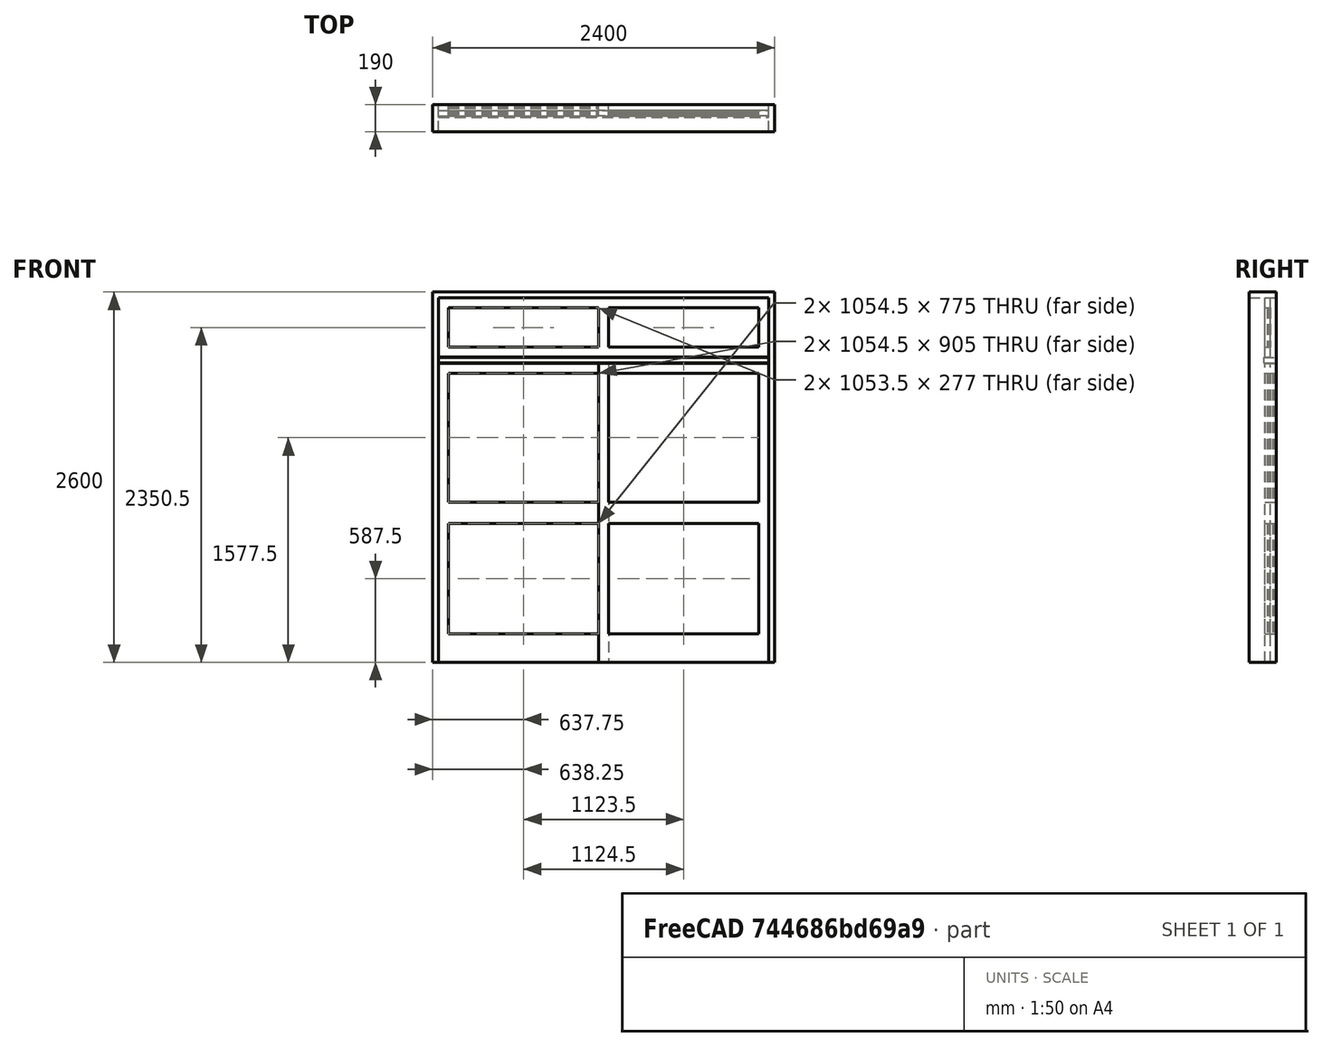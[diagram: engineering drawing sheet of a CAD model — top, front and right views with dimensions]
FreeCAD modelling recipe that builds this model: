
FCSTD DOCUMENT  (FreeCAD 0.16R6704 (Git))
Label: slinding double doors with glass and transom
License: CreativeCommons Attribution
LicenseURL: http://creativecommons.org/licenses/by/4.0/
objects: Sketcher::SketchObject×1, Part::FeaturePython×1
note: 2 computed .brp shape members not serialized (recipe doc carries the construction recipe); baked Part::Feature solids carry a one-line shape summary decoded from their .brp

FEATURE [Sketcher::SketchObject] Sketch180
  Placement = pos=(0,0,0) rot=(1,0,0;1.5708rad)
  sketch-geometry (50):
    g0: LineSegment StartX=0 StartY=0 StartZ=0 EndX=2400 EndY=0 EndZ=0
    g1: LineSegment StartX=2400 StartY=0 StartZ=0 EndX=2400 EndY=2600 EndZ=0
    g2: LineSegment StartX=2400 StartY=2600 StartZ=0 EndX=0 EndY=2600 EndZ=0
    g3: LineSegment StartX=0 StartY=2600 StartZ=0 EndX=0 EndY=0 EndZ=0
    g4: LineSegment StartX=40 StartY=0 StartZ=0 EndX=2360 EndY=0 EndZ=0
    g5: LineSegment StartX=2360 StartY=0 StartZ=0 EndX=2360 EndY=2560 EndZ=0
    g6: LineSegment StartX=2360 StartY=2560 StartZ=0 EndX=40 EndY=2560 EndZ=0
    g7: LineSegment StartX=40 StartY=2560 StartZ=0 EndX=40 EndY=0 EndZ=0
    g8: LineSegment StartX=111 StartY=2030 StartZ=0 EndX=1165.5 EndY=2030 EndZ=0
    g9: LineSegment StartX=1165.5 StartY=2030 StartZ=0 EndX=1165.5 EndY=1125 EndZ=0
    g10: LineSegment StartX=1165.5 StartY=1125 StartZ=0 EndX=111 EndY=1125 EndZ=0
    g11: LineSegment StartX=111 StartY=1125 StartZ=0 EndX=111 EndY=2030 EndZ=0
    g12: LineSegment StartX=111 StartY=975 StartZ=0 EndX=1165.5 EndY=975 EndZ=0
    g13: LineSegment StartX=1165.5 StartY=975 StartZ=0 EndX=1165.5 EndY=200 EndZ=0
    g14: LineSegment StartX=1165.5 StartY=200 StartZ=0 EndX=111 EndY=200 EndZ=0
    g15: LineSegment StartX=111 StartY=200 StartZ=0 EndX=111 EndY=975 EndZ=0
    g16: LineSegment [constr] StartX=-278 StartY=1050 StartZ=0 EndX=2205 EndY=1050 EndZ=0
    g17: LineSegment StartX=41 StartY=2100 StartZ=0 EndX=1235.5 EndY=2100 EndZ=0
    g18: LineSegment StartX=1235.5 StartY=2100 StartZ=0 EndX=1235.5 EndY=1 EndZ=0
    g19: LineSegment StartX=1235.5 StartY=1 StartZ=0 EndX=41 EndY=1 EndZ=0
    g20: LineSegment StartX=41 StartY=1 StartZ=0 EndX=41 EndY=2100 EndZ=0
    g21: LineSegment [constr] StartX=1200 StartY=2318.59 StartZ=0 EndX=1200 EndY=-187.261 EndZ=0
    g22: LineSegment StartX=2289 StartY=2030 StartZ=0 EndX=1234.5 EndY=2030 EndZ=0
    g23: LineSegment StartX=1234.5 StartY=2030 StartZ=0 EndX=1234.5 EndY=1125 EndZ=0
    g24: LineSegment StartX=1234.5 StartY=1125 StartZ=0 EndX=2289 EndY=1125 EndZ=0
    g25: LineSegment StartX=2289 StartY=1125 StartZ=0 EndX=2289 EndY=2030 EndZ=0
    g26: LineSegment StartX=2289 StartY=975 StartZ=0 EndX=1234.5 EndY=975 EndZ=0
    g27: LineSegment StartX=1234.5 StartY=975 StartZ=0 EndX=1234.5 EndY=200 EndZ=0
    g28: LineSegment StartX=1234.5 StartY=200 StartZ=0 EndX=2289 EndY=200 EndZ=0
    g29: LineSegment StartX=2289 StartY=200 StartZ=0 EndX=2289 EndY=975 EndZ=0
    g30: LineSegment StartX=2359 StartY=2100 StartZ=0 EndX=1164.5 EndY=2100 EndZ=0
    g31: LineSegment StartX=1164.5 StartY=2100 StartZ=0 EndX=1164.5 EndY=1 EndZ=0
    g32: LineSegment StartX=1164.5 StartY=1 StartZ=0 EndX=2359 EndY=1 EndZ=0
    g33: LineSegment StartX=2359 StartY=1 StartZ=0 EndX=2359 EndY=2100 EndZ=0
    g34: LineSegment StartX=41 StartY=2559 StartZ=0 EndX=2359 EndY=2559 EndZ=0
    g35: LineSegment StartX=2359 StartY=2559 StartZ=0 EndX=2359 EndY=2142 EndZ=0
    g36: LineSegment StartX=2359 StartY=2142 StartZ=0 EndX=41 EndY=2142 EndZ=0
    g37: LineSegment StartX=41 StartY=2142 StartZ=0 EndX=41 EndY=2559 EndZ=0
    g38: LineSegment StartX=111 StartY=2489 StartZ=0 EndX=1164.5 EndY=2489 EndZ=0
    g39: LineSegment StartX=1164.5 StartY=2489 StartZ=0 EndX=1164.5 EndY=2212 EndZ=0
    g40: LineSegment StartX=1164.5 StartY=2212 StartZ=0 EndX=111 EndY=2212 EndZ=0
    g41: LineSegment StartX=111 StartY=2212 StartZ=0 EndX=111 EndY=2489 EndZ=0
    g42: LineSegment StartX=1235.5 StartY=2489 StartZ=0 EndX=2289 EndY=2489 EndZ=0
    g43: LineSegment StartX=2289 StartY=2489 StartZ=0 EndX=2289 EndY=2212 EndZ=0
    g44: LineSegment StartX=2289 StartY=2212 StartZ=0 EndX=1235.5 EndY=2212 EndZ=0
    g45: LineSegment StartX=1235.5 StartY=2212 StartZ=0 EndX=1235.5 EndY=2489 EndZ=0
    g46: LineSegment StartX=41 StartY=2141 StartZ=0 EndX=2359 EndY=2141 EndZ=0
    g47: LineSegment StartX=2359 StartY=2141 StartZ=0 EndX=2359 EndY=2101 EndZ=0
    g48: LineSegment StartX=2359 StartY=2101 StartZ=0 EndX=41 EndY=2101 EndZ=0
    g49: LineSegment StartX=41 StartY=2101 StartZ=0 EndX=41 EndY=2141 EndZ=0
  constraints (146):
    c: Coincident(g0,g1)
    c: Coincident(g1,g2)
    c: Coincident(g2,g3)
    c: Coincident(g3,g0)
    c: Horizontal(g0)
    c: Horizontal(g2)
    c: Vertical(g1)
    c: Vertical(g3)
    c: Coincident(g4,g5)
    c: Coincident(g5,g6)
    c: Coincident(g6,g7)
    c: Coincident(g7,g4)
    c: Horizontal(g4)
    c: Horizontal(g6)
    c: Vertical(g5)
    c: Vertical(g7)
    c: DistanceY(g1) = 2600  'Altura do vão'
    c: DistanceX(g0) = 2400  'Largura do vão'
    c: DistanceY(g6,g2) = 40  'Altura batente superior'
    c: DistanceX(g2,g6) = 40  'Largura do batente 1'
    c: DistanceX(g4,g0) = 40  'Largura do batente 2'
    c: DistanceY(g0,g4) = 0
    c: Coincident(g0,g-1)
    c: Coincident(g8,g9)
    c: Coincident(g9,g10)
    c: Coincident(g10,g11)
    c: Coincident(g11,g8)
    c: Horizontal(g8)
    c: Horizontal(g10)
    c: Vertical(g9)
    c: Vertical(g11)
    c: Coincident(g12,g13)
    c: Coincident(g13,g14)
    c: Coincident(g14,g15)
    c: Coincident(g15,g12)
    c: Horizontal(g12)
    c: Horizontal(g14)
    c: Vertical(g13)
    c: Vertical(g15)
    c: DistanceX(g10,g12) = 0
    c: DistanceX(g9,g12) = 0
    c: DistanceY(g12,g10) = 150  'Altura do montante intermediário porta'
    c: DistanceY(g-1,g14) = 200  'Altura moldura inferior porta'
    c: Horizontal(g16)
    c: Symmetric(g10,g12,g16)
    c: DistanceY(g-1,g16) = 1050  'Altura da divisão intermediária porta'
    c: Coincident(g17,g18)
    c: Coincident(g18,g19)
    c: Coincident(g19,g20)
    c: Horizontal(g17)
    c: Horizontal(g19)
    c: Vertical(g18)
    c: Vertical(g20)
    c: DistanceY(g4,g18) = 1
    c: DistanceX(g6,g17) = 1
    c: Vertical(g21)  'Constraint59'
    c: Symmetric(g2,g1,g21)  'Constraint58'
    c: Coincident(g22,g23)
    c: Coincident(g23,g24)
    c: Coincident(g24,g25)
    c: Coincident(g25,g22)
    c: Horizontal(g22)
    c: Horizontal(g24)
    c: Vertical(g23)
    c: Vertical(g25)
    c: Coincident(g26,g27)
    c: Coincident(g27,g28)
    c: Coincident(g28,g29)
    c: Coincident(g29,g26)
    c: Horizontal(g26)
    c: Horizontal(g28)
    c: Vertical(g27)
    c: Vertical(g29)
    c: Coincident(g30,g31)
    c: Coincident(g31,g32)
    c: Coincident(g32,g33)
    c: Horizontal(g30)
    c: Horizontal(g32)
    c: Vertical(g31)
    c: Vertical(g33)
    c: DistanceX(g30,g5) = 1
    c: DistanceY(g8,g22) = 0
    c: DistanceY(g9,g23) = 0
    c: DistanceY(g26,g12) = 0
    c: DistanceY(g18,g31) = 0
    c: Symmetric(g8,g22,g21)
    c: DistanceX(g24,g26) = 0
    c: Coincident(g30,g33)
    c: DistanceY(g8,g17) = 70  'Altura moldura porta'
    c: Coincident(g34,g35)  'Constraint94'
    c: Coincident(g35,g36)  'Constraint93'
    c: Coincident(g36,g37)  'Constraint92'
    c: Coincident(g37,g34)
    c: Horizontal(g34)
    c: Horizontal(g36)
    c: Vertical(g35)
    c: Vertical(g37)
    c: Coincident(g38,g39)
    c: Coincident(g39,g40)
    c: Coincident(g40,g41)
    c: Coincident(g41,g38)
    c: Horizontal(g38)
    c: Horizontal(g40)
    c: Vertical(g39)
    c: Vertical(g41)
    c: Coincident(g42,g43)
    c: Coincident(g43,g44)
    c: Coincident(g44,g45)
    c: Coincident(g45,g42)
    c: Horizontal(g42)
    c: Horizontal(g44)
    c: Vertical(g43)
    c: Vertical(g45)
    c: Coincident(g46,g47)
    c: Coincident(g47,g48)
    c: Coincident(g48,g49)
    c: Coincident(g49,g46)
    c: Horizontal(g46)
    c: Horizontal(g48)
    c: Vertical(g47)
    c: Vertical(g49)
    c: DistanceX(g17,g48) = 0
    c: DistanceX(g47,g30) = 0
    c: DistanceY(g17,g48) = 1  'Constraint129'
    c: DistanceY(g47,g46) = 40  'Batente bandeira'
    c: DistanceY(g46,g35) = 1  'Constraint127'
    c: DistanceX(g35,g46) = 0
    c: DistanceX(g46,g36) = 0
    c: DistanceY(g34,g6) = 1
    c: DistanceX(g40,g8) = 0
    c: DistanceY(g36,g40) = 70  'Moldura inferior bandeira'
    c: DistanceY(g39,g44) = 0  'Constraint132'
    c: DistanceX(g43,g22) = 0
    c: DistanceY(g38,g42) = 0
    c: DistanceY(g38,g34) = 70  'Altura moldura superior bandeira'
    c: DistanceY(g-1,g17) = 2100  'Altura porta'
    c: Coincident(g17,g20)
    c: DistanceY(g27,g13) = 0
    c: DistanceX(g17,g8) = 70  'Largura montante vertica porta 1'
    c: DistanceX(g30,g22) = 70  'Montante vertical 1 porta 2'
    c: DistanceX(g8,g17) = 70  'Montante vertical 2 porta 1'
    c: DistanceX(g30,g8) = 1  'Constraint143'
    c: Symmetric(g30,g17,g21)
    c: DistanceX(g23,g26) = 0
    c: DistanceX(g39,g30) = 0
    c: DistanceX(g17,g44) = 0
FEATURE [Part::FeaturePython] Window113  label="Slinding double doors with glass and transom"  # WARN: FeaturePython — macro-defined, semantics opaque (R4)
  Base = -> Sketch180
  Height = 2100
  HoleDepth = 0
  MoveWithHost = true
  Normal = (0,1,0)
  Preset = 6
  Role = 1
  Width = 900
  WindowParts = BATENTE | Frame | Wire0,Wire1 | 190.0 | 0.0 | PORTA 1 | Frame | Wire2,Wire3,Wire4 | 40.0 | 150.0 | PORTA 2 | Frame | Wire5,Wire6,Wire7 | 40.0 | 110.0 | BATENTE BANDEIRA | Frame | Wire11 | 90.0 | 100.0 | BANDEIRA | Frame | Wire10,Wire9,Wire8 | 40.0 | 110.0 | VIDRO 1 BANDEIRA | Glass panel | Wire9 | 10.0 | 125.0 | VIDRO 2 BANDEIRA | Glass panel | Wire10 | 10.0 | 125.0 | VIDRO SUPERIOR PORTA 1 | Glass panel | Wire2 | 10.0 | 165.0 | VIDRO SUPERIOR PORTA 2 | Glass panel | Wire5 | 10.0 | 125.0 | VIDRO INFERIOR PORTA 1 | Glass panel | Wire3 | 10.0 | 165.0 | VIDRO INFERIOR PORTA 2 | Glass panel | Wire6 | 10.0 | 125.0
